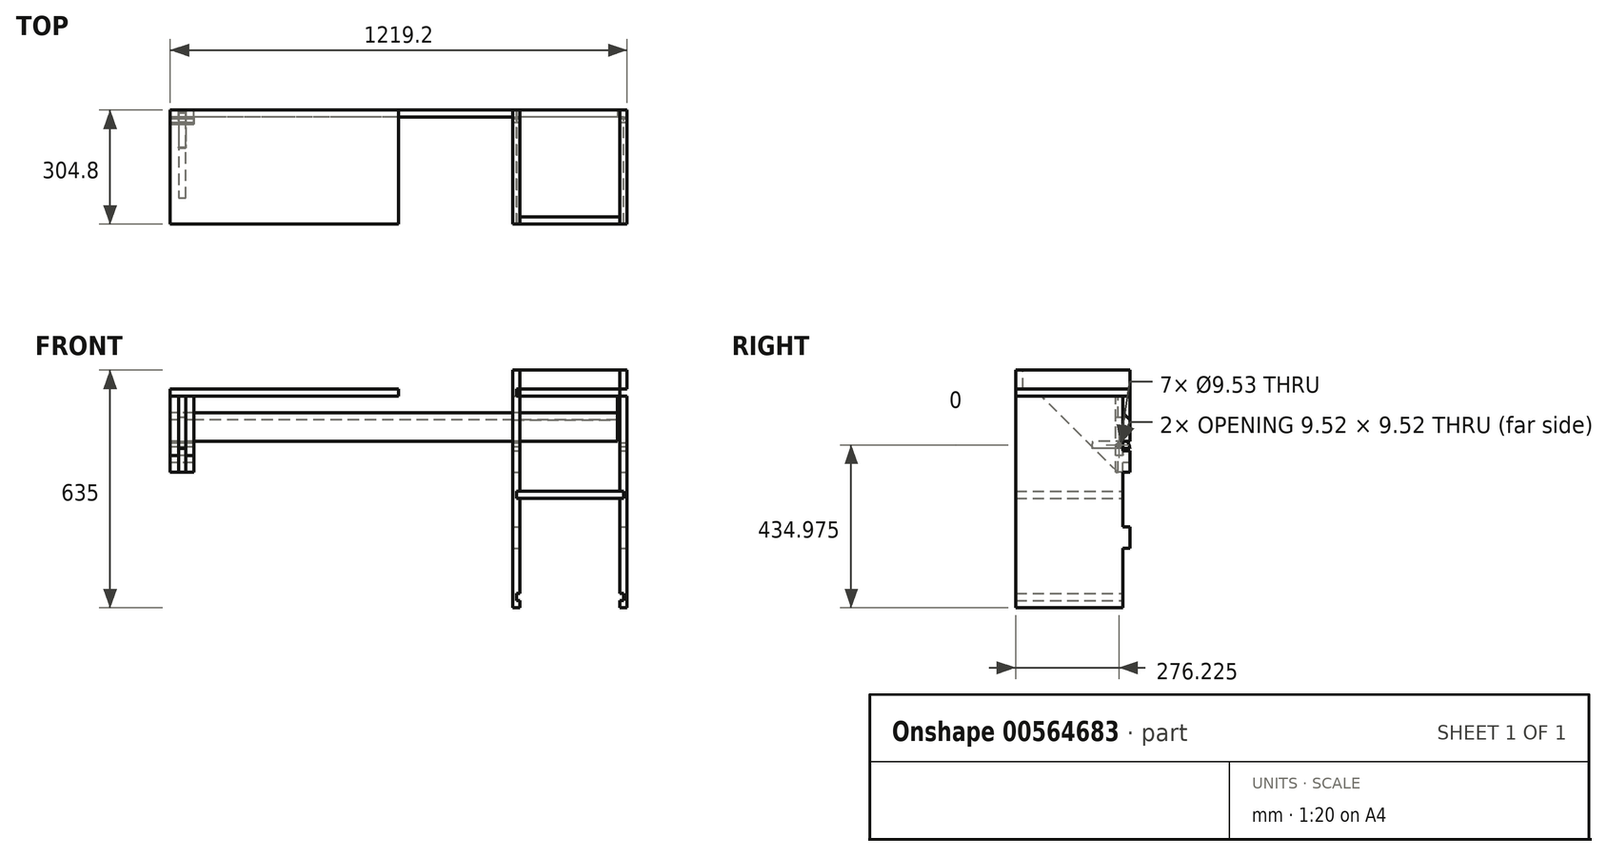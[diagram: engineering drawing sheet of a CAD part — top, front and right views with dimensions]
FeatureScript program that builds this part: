
annotation { "Feature Type Name" : "Feature", "Feature Type Description" : "" }
export const myFeature = defineFeature(function(context is Context, id is Id, definition is map)
    precondition{}
    {
        {
            var Q0;
            Q0=qCreatedBy(makeId("Right.planeOp"),FACE);
            var sketch = newSketch(context, id + "F0", { "sketchPlane" : qUnion([Q0])});
            skLineSegment(sketch, "E0", {"start": v(0, 0) * mm, "end": v(0, 57.15) * mm});
            skLineSegment(sketch, "E1", {"start": v(0, 57.15) * mm, "end": v(-19.05, 76.2) * mm});
            skLineSegment(sketch, "E2", {"start": v(-19.05, 76.2) * mm, "end": v(-19.05, 0) * mm});
            skLineSegment(sketch, "E3", {"start": v(-19.05, 0) * mm, "end": v(0, 0) * mm});
            skSolve(sketch);
        }
        {
            var Q0;
            Q0=makeQuery(id+"F0.imprint","IMPRINT",FACE,{"disambiguationData":[TD([[makeQuery(id+"F0.imprint","IMPRINT",EDGE,{"derivedFrom":sQuery(id+"F0.wireOp",EDGE,"E0")}),1.0]])]});
            extrude(context, id + "F1", {"entities" : qUnion([Q0]), "depth" : 1219.2 * mm, "offsetDistance" : 25.4 * mm});
        }
        {
            var Q0;
            Q0=qCreatedBy(makeId("Right.planeOp"),FACE);
            var sketch = newSketch(context, id + "F2", { "sketchPlane" : qUnion([Q0])});
            skLineSegment(sketch, "E4", {"start": v(0, 57.15) * mm, "end": v(0, 120.65) * mm});
            skLineSegment(sketch, "E5", {"start": v(0, 120.65) * mm, "end": v(-19.05, 120.65) * mm});
            skLineSegment(sketch, "E6", {"start": v(-19.05, 120.65) * mm, "end": v(-19.05, 76.2) * mm});
            skLineSegment(sketch, "E7", {"start": v(-19.05, 76.2) * mm, "end": v(0, 57.15) * mm});
            skSolve(sketch);
        }
        {
            var Q0;
            Q0=makeQuery(id+"F2.imprint","IMPRINT",FACE,{"disambiguationData":[TD([[makeQuery(id+"F2.imprint","IMPRINT",EDGE,{"derivedFrom":sQuery(id+"F2.wireOp",EDGE,"E4")}),1.0]])]});
            extrude(context, id + "F3", {"entities" : qUnion([Q0]), "depth" : 63.5 * mm, "offsetDistance" : 25.4 * mm});
        }
        {
            var Q0;
            Q0=makeQuery(id+"F3.opExtrude","SWEPT_FACE",FACE,{"disambiguationData":[OSD([sQuery(id+"F2.wireOp",EDGE,"E5")])]});
            var sketch = newSketch(context, id + "F4", { "sketchPlane" : qUnion([Q0])});
            skLineSegment(sketch, "E8.bottom", {"start": v(0, -19.05) * mm, "end": v(63.5, -19.05) * mm});
            skLineSegment(sketch, "E8.top", {"start": v(0, -38.1) * mm, "end": v(63.5, -38.1) * mm});
            skLineSegment(sketch, "E8.left", {"start": v(0, -19.05) * mm, "end": v(0, -38.1) * mm});
            skLineSegment(sketch, "E8.right", {"start": v(63.5, -19.05) * mm, "end": v(63.5, -38.1) * mm});
            skSolve(sketch);
        }
        {
            var Q0;
            Q0=makeQuery(id+"F4.imprint","IMPRINT",FACE,{"disambiguationData":[TD([[makeQuery(id+"F4.imprint","IMPRINT",EDGE,{"derivedFrom":sQuery(id+"F4.wireOp",EDGE,"E8.bottom")}),1.0]])]});
            extrude(context, id + "F5", {"entities" : qUnion([Q0]), "oppositeDirection" : true, "depth" : 203.2 * mm, "offsetDistance" : 25.4 * mm});
        }
        {
            var Q0;
            Q0=makeQuery(id+"F5.opExtrude","CAP_FACE",FACE,{"disambiguationData":[OSD([sQuery(id+"F4.wireOp",EDGE,"E8.bottom"),sQuery(id+"F4.wireOp",EDGE,"E8.top"),sQuery(id+"F4.wireOp",EDGE,"E8.left"),sQuery(id+"F4.wireOp",EDGE,"E8.right")])],"isStart":true});
            var sketch = newSketch(context, id + "F6", { "sketchPlane" : qUnion([Q0])});
            skLineSegment(sketch, "E9.bottom", {"start": v(22.23, -38.1) * mm, "end": v(41.28, -38.1) * mm});
            skLineSegment(sketch, "E9.top", {"start": v(22.23, -31.75) * mm, "end": v(41.28, -31.75) * mm});
            skLineSegment(sketch, "E9.left", {"start": v(22.23, -38.1) * mm, "end": v(22.23, -31.75) * mm});
            skLineSegment(sketch, "E9.right", {"start": v(41.28, -38.1) * mm, "end": v(41.28, -31.75) * mm});
            skSolve(sketch);
        }
        {
            var Q0;
            Q0=makeQuery(id+"F6.imprint","IMPRINT",FACE,{"disambiguationData":[TD([[makeQuery(id+"F6.imprint","IMPRINT",EDGE,{"derivedFrom":sQuery(id+"F6.wireOp",EDGE,"E9.bottom")}),1.0]])]});
            extrude(context, id + "F7", {"entities" : qUnion([Q0]), "operationType" : NewBodyOperationType.REMOVE, "endBound" : BoundingType.THROUGH_ALL, "oppositeDirection" : true, "depth" : 25.4 * mm, "offsetDistance" : 25.4 * mm});
        }
        {
            var Q0;
            Q0=makeQuery(id+"F7.boolean.opBoolean","COPY",FACE,{"derivedFrom":makeQuery(id+"F7.opExtrude","SWEPT_FACE",FACE,{"disambiguationData":[OSD([sQuery(id+"F6.wireOp",EDGE,"E9.right")])]})});
            var sketch = newSketch(context, id + "F8", { "sketchPlane" : qUnion([Q0])});
            skLineSegment(sketch, "E10", {"start": v(31.75, 120.65) * mm, "end": v(31.75, -82.55) * mm});
            skLineSegment(sketch, "E11", {"start": v(31.75, -82.55) * mm, "end": v(234.95, 120.65) * mm});
            skPoint(sketch, "E11.endSnap0", {"position": v(34.93, 120.65) * mm});
            skLineSegment(sketch, "E12", {"start": v(234.95, 120.65) * mm, "end": v(31.75, 120.65) * mm});
            skSolve(sketch);
        }
        {
            var Q0;
            Q0 = qSketchRegion(id + "F8", true);
            extrude(context, id + "F9", {"entities" : qUnion([Q0]), "depth" : 19.05 * mm, "offsetDistance" : 25.4 * mm});
        }
        {
            var Q0;
            Q0=qCreatedBy(makeId("Right.planeOp"),FACE);
            var sketch = newSketch(context, id + "F10", { "sketchPlane" : qUnion([Q0])});
            skLineSegment(sketch, "E13.bottom", {"start": v(0, 120.65) * mm, "end": v(-279.4, 120.65) * mm});
            skLineSegment(sketch, "E13.top", {"start": v(0, 139.7) * mm, "end": v(-279.4, 139.7) * mm});
            skLineSegment(sketch, "E13.left", {"start": v(0, 120.65) * mm, "end": v(0, 139.7) * mm});
            skLineSegment(sketch, "E13.right", {"start": v(-279.4, 120.65) * mm, "end": v(-279.4, 139.7) * mm});
            skSolve(sketch);
        }
        {
            var Q0;
            Q0=makeQuery(id+"F10.imprint","IMPRINT",FACE,{"disambiguationData":[TD([[makeQuery(id+"F10.imprint","IMPRINT",EDGE,{"derivedFrom":sQuery(id+"F10.wireOp",EDGE,"E13.bottom")}),-1.0]])]});
            extrude(context, id + "F11", {"entities" : qUnion([Q0]), "depth" : 609.6 * mm, "offsetDistance" : 25.4 * mm});
        }
        {
            var Q0;
            Q0=makeQuery(id+"F5.opExtrude","SWEPT_FACE",FACE,{"disambiguationData":[OSD([sQuery(id+"F4.wireOp",EDGE,"E8.bottom")])]});
            var sketch = newSketch(context, id + "F12", { "sketchPlane" : qUnion([Q0])});
            skLineSegment(sketch, "E14.bottom", {"start": v(-63.5, -82.55) * mm, "end": v(0, -82.55) * mm});
            skLineSegment(sketch, "E14.top", {"start": v(-63.5, -57.15) * mm, "end": v(0, -57.15) * mm});
            skLineSegment(sketch, "E14.left", {"start": v(-63.5, -82.55) * mm, "end": v(-63.5, -57.15) * mm});
            skLineSegment(sketch, "E14.right", {"start": v(0, -82.55) * mm, "end": v(0, -57.15) * mm});
            skSolve(sketch);
        }
        {
            var Q0;
            Q0=makeQuery(id+"F12.imprint","IMPRINT",FACE,{"disambiguationData":[TD([[makeQuery(id+"F12.imprint","IMPRINT",EDGE,{"derivedFrom":sQuery(id+"F12.wireOp",EDGE,"E14.bottom")}),1.0]])]});
            extrude(context, id + "F13", {"entities" : qUnion([Q0]), "depth" : 19.05 * mm, "offsetDistance" : 25.4 * mm});
        }
        {
            var Q0;
            Q0=makeQuery(id+"F11.opExtrude","SWEPT_FACE",FACE,{"disambiguationData":[OSD([sQuery(id+"F10.wireOp",EDGE,"E13.right")])]});
            extrude(context, id + "F14", {"entities" : qUnion([Q0]), "operationType" : NewBodyOperationType.ADD, "depth" : 25.4 * mm, "offsetDistance" : 25.4 * mm});
        }
        {
            var Q0;
            Q0=makeQuery(id+"F1.opExtrude","CAP_FACE",FACE,{"disambiguationData":[OSD([sQuery(id+"F0.wireOp",EDGE,"E0"),sQuery(id+"F0.wireOp",EDGE,"E1"),sQuery(id+"F0.wireOp",EDGE,"E2"),sQuery(id+"F0.wireOp",EDGE,"E3")])],"isStart":false});
            var sketch = newSketch(context, id + "F15", { "sketchPlane" : qUnion([Q0])});
            skLineSegment(sketch, "E15", {"start": v(0, 57.15) * mm, "end": v(-19.05, 76.2) * mm});
            skLineSegment(sketch, "E16", {"start": v(-19.05, 76.2) * mm, "end": v(-19.05, 120.65) * mm});
            skLineSegment(sketch, "E17", {"start": v(-19.05, 120.65) * mm, "end": v(0, 120.65) * mm});
            skLineSegment(sketch, "E18", {"start": v(0, 120.65) * mm, "end": v(0, 57.15) * mm});
            skSolve(sketch);
        }
        {
            var Q0;
            Q0=makeQuery(id+"F15.imprint","IMPRINT",FACE,{"disambiguationData":[TD([[makeQuery(id+"F15.imprint","IMPRINT",EDGE,{"derivedFrom":sQuery(id+"F15.wireOp",EDGE,"E15")}),-1.0]])]});
            extrude(context, id + "F16", {"entities" : qUnion([Q0]), "oppositeDirection" : true, "depth" : 304.8 * mm, "offsetDistance" : 25.4 * mm});
        }
        {
            var Q0;
            Q0=makeQuery(id+"F16.opExtrude","CAP_FACE",FACE,{"disambiguationData":[OSD([sQuery(id+"F15.wireOp",EDGE,"E15"),sQuery(id+"F15.wireOp",EDGE,"E16"),sQuery(id+"F15.wireOp",EDGE,"E17"),sQuery(id+"F15.wireOp",EDGE,"E18")])],"isStart":true});
            var sketch = newSketch(context, id + "F17", { "sketchPlane" : qUnion([Q0])});
            skLineSegment(sketch, "E19.bottom", {"start": v(0, 120.65) * mm, "end": v(-304.8, 120.65) * mm});
            skLineSegment(sketch, "E19.top", {"start": v(0, 139.7) * mm, "end": v(-304.8, 139.7) * mm});
            skLineSegment(sketch, "E19.left", {"start": v(0, 120.65) * mm, "end": v(0, 139.7) * mm});
            skLineSegment(sketch, "E19.right", {"start": v(-304.8, 120.65) * mm, "end": v(-304.8, 139.7) * mm});
            skSolve(sketch);
        }
        {
            var Q0;
            Q0=makeQuery(id+"F17.imprint","IMPRINT",FACE,{"disambiguationData":[TD([[makeQuery(id+"F17.imprint","IMPRINT",EDGE,{"derivedFrom":sQuery(id+"F17.wireOp",EDGE,"E19.top")}),1.0]])]});
            extrude(context, id + "F18", {"entities" : qUnion([Q0]), "oppositeDirection" : true, "depth" : 304.8 * mm, "offsetDistance" : 25.4 * mm});
        }
        {
            var Q0;
            Q0=makeQuery(id+"F16.opExtrude","CAP_FACE",FACE,{"disambiguationData":[OSD([sQuery(id+"F15.wireOp",EDGE,"E15"),sQuery(id+"F15.wireOp",EDGE,"E16"),sQuery(id+"F15.wireOp",EDGE,"E17"),sQuery(id+"F15.wireOp",EDGE,"E18")])],"isStart":true});
            var sketch = newSketch(context, id + "F19", { "sketchPlane" : qUnion([Q0])});
            skLineSegment(sketch, "E20.bottom", {"start": v(-304.8, 165.1) * mm, "end": v(0, 165.1) * mm});
            skLineSegment(sketch, "E20.top", {"start": v(-304.8, -444.5) * mm, "end": v(0, -444.5) * mm});
            skLineSegment(sketch, "E20.left", {"start": v(-304.8, 165.1) * mm, "end": v(-304.8, -444.5) * mm});
            skLineSegment(sketch, "E20.right", {"start": v(0, 165.1) * mm, "end": v(0, -444.5) * mm});
            skSolve(sketch);
        }
        {
            var Q0;
            {var subQ1=makeQuery(id+"F16.opExtrude","CAP_EDGE",EDGE,{"disambiguationData":[OSD([sQuery(id+"F15.wireOp",EDGE,"E15")])],"isStart":true});Q0=makeQuery(id+"F19.imprint","IMPRINT",FACE,{"disambiguationData":[TD([[makeQuery(id+"F19.imprint","IMPRINT",EDGE,{"derivedFrom":subQ1}),-1.0]])]});}
            var Q1;
            {var subQ2=sQuery(id+"F19.wireOp",EDGE,"E20.bottom");Q1=makeQuery(id+"F19.imprint","IMPRINT",FACE,{"disambiguationData":[TD([[makeQuery(id+"F19.imprint","IMPRINT",EDGE,{"derivedFrom":subQ2}),-1.0]])]});}
            extrude(context, id + "F20", {"entities" : qUnion([Q0, Q1]), "oppositeDirection" : true, "depth" : 19.05 * mm, "offsetDistance" : 25.4 * mm});
        }
        {
            var Q0;
            Q0=makeQuery(id+"F20.opExtrude","SWEPT_FACE",FACE,{"disambiguationData":[OSD([sQuery(id+"F19.wireOp",EDGE,"E20.bottom")])]});
            extrude(context, id + "F21", {"entities" : qUnion([Q0]), "operationType" : NewBodyOperationType.ADD, "depth" : 25.4 * mm, "offsetDistance" : 25.4 * mm});
        }
        {
            var Q0;
            {var subQ0=sQuery(id+"F19.wireOp",EDGE,"E20.bottom");Q0=makeQuery(id+"F21.boolean.opBoolean","MERGE",FACE,{"derivedFrom":[makeQuery(id+"F20.opExtrude","CAP_FACE",FACE,{"disambiguationData":[OSD([subQ0,sQuery(id+"F19.wireOp",EDGE,"E20.top"),sQuery(id+"F19.wireOp",EDGE,"E20.left"),sQuery(id+"F19.wireOp",EDGE,"E20.right")])],"isStart":true}),makeQuery(id+"F21.opExtrude","SWEPT_FACE",FACE,{"disambiguationData":[OSD([subQ0]),TDD([makeQuery(id+"F20.opExtrude","CAP_EDGE",EDGE,{"disambiguationData":[OSD([subQ0])],"isStart":true})])]})]});}
            var sketch = newSketch(context, id + "F22", { "sketchPlane" : qUnion([Q0])});
            skLineSegment(sketch, "E21.bottom", {"start": v(0, 120.65) * mm, "end": v(-19.05, 120.65) * mm});
            skLineSegment(sketch, "E21.top", {"start": v(0, -25.4) * mm, "end": v(-19.05, -25.4) * mm});
            skLineSegment(sketch, "E21.left", {"start": v(0, 120.65) * mm, "end": v(0, -25.4) * mm});
            skLineSegment(sketch, "E21.right", {"start": v(-19.05, 120.65) * mm, "end": v(-19.05, -25.4) * mm});
            skLineSegment(sketch, "E22.bottom", {"start": v(0, -82.55) * mm, "end": v(-19.05, -82.55) * mm});
            skLineSegment(sketch, "E22.top", {"start": v(0, -228.6) * mm, "end": v(-19.05, -228.6) * mm});
            skLineSegment(sketch, "E22.left", {"start": v(0, -82.55) * mm, "end": v(0, -228.6) * mm});
            skLineSegment(sketch, "E22.right", {"start": v(-19.05, -82.55) * mm, "end": v(-19.05, -228.6) * mm});
            skLineSegment(sketch, "E23.bottom", {"start": v(0, -285.75) * mm, "end": v(-19.05, -285.75) * mm});
            skLineSegment(sketch, "E23.top", {"start": v(0, -444.5) * mm, "end": v(-19.05, -444.5) * mm});
            skLineSegment(sketch, "E23.left", {"start": v(0, -285.75) * mm, "end": v(0, -444.5) * mm});
            skLineSegment(sketch, "E23.right", {"start": v(-19.05, -285.75) * mm, "end": v(-19.05, -444.5) * mm});
            skSolve(sketch);
        }
        {
            var Q0;
            Q0 = qSketchRegion(id + "F22", true);
            extrude(context, id + "F23", {"entities" : qUnion([Q0]), "operationType" : NewBodyOperationType.REMOVE, "oppositeDirection" : true, "depth" : 25.4 * mm, "offsetDistance" : 25.4 * mm});
        }
        {
            var Q0;
            Q0=makeQuery(id+"F18.opExtrude","CAP_FACE",FACE,{"disambiguationData":[OSD([sQuery(id+"F17.wireOp",EDGE,"E19.bottom"),sQuery(id+"F17.wireOp",EDGE,"E19.top"),sQuery(id+"F17.wireOp",EDGE,"E19.left"),sQuery(id+"F17.wireOp",EDGE,"E19.right")])],"isStart":true});
            extrude(context, id + "F24", {"entities" : qUnion([Q0]), "operationType" : NewBodyOperationType.REMOVE, "oppositeDirection" : true, "depth" : 9.52 * mm, "offsetDistance" : 25.4 * mm});
        }
        {
            var Q0;
            Q0=makeQuery(id+"F18.opExtrude","CAP_FACE",FACE,{"disambiguationData":[OSD([sQuery(id+"F17.wireOp",EDGE,"E19.bottom"),sQuery(id+"F17.wireOp",EDGE,"E19.top"),sQuery(id+"F17.wireOp",EDGE,"E19.left"),sQuery(id+"F17.wireOp",EDGE,"E19.right")])],"isStart":false});
            extrude(context, id + "F25", {"entities" : qUnion([Q0]), "operationType" : NewBodyOperationType.REMOVE, "oppositeDirection" : true, "depth" : 9.52 * mm, "offsetDistance" : 25.4 * mm});
        }
        {
            var Q0;
            Q0=makeQuery(id+"F20.opExtrude","SWEPT_BODY",BODY,{"disambiguationData":[OSD([sQuery(id+"F19.wireOp",EDGE,"E20.bottom"),sQuery(id+"F19.wireOp",EDGE,"E20.top"),sQuery(id+"F19.wireOp",EDGE,"E20.left"),sQuery(id+"F19.wireOp",EDGE,"E20.right")])]});
            transform(context, id + "F26", {"entities" : qUnion([Q0]), "transformType" : TransformType.TRANSLATION_3D, "dx" : -285.75 * mm, "dy" : 0 * mm, "dz" : 0 * mm, "makeCopy" : true});
        }
        {
            var Q0;
            {var subQ0=sQuery(id+"F19.wireOp",EDGE,"E20.bottom");var subQ1=sQuery(id+"F19.wireOp",EDGE,"E20.right");Q0=makeQuery(id+"F23.boolean.opBoolean","SPLIT",FACE,{"disambiguationData":[TD([makeQuery(id+"F21.opExtrude","CAP_FACE",FACE,{"disambiguationData":[OSD([subQ0])],"isStart":false})])],"derivedFrom":makeQuery(id+"F21.boolean.opBoolean","MERGE",FACE,{"derivedFrom":[makeQuery(id+"F20.opExtrude","SWEPT_FACE",FACE,{"disambiguationData":[OSD([subQ1])]}),makeQuery(id+"F21.opExtrude","SWEPT_FACE",FACE,{"disambiguationData":[OSD([subQ0,subQ1])]})]})});}
            var sketch = newSketch(context, id + "F27", { "sketchPlane" : qUnion([Q0])});
            skLineSegment(sketch, "E24.bottom", {"start": v(-1200.15, 120.65) * mm, "end": v(-1209.67, 120.65) * mm});
            skLineSegment(sketch, "E24.top", {"start": v(-1200.15, 139.7) * mm, "end": v(-1209.67, 139.7) * mm});
            skLineSegment(sketch, "E24.left", {"start": v(-1200.15, 120.65) * mm, "end": v(-1200.15, 139.7) * mm});
            skLineSegment(sketch, "E24.right", {"start": v(-1209.67, 120.65) * mm, "end": v(-1209.67, 139.7) * mm});
            skLineSegment(sketch, "E25.0.1.0", {"start": v(-1209.67, -152.4) * mm, "end": v(-1209.67, -133.35) * mm});
            skLineSegment(sketch, "E25.0.1.1", {"start": v(-1200.15, -133.35) * mm, "end": v(-1209.67, -133.35) * mm});
            skLineSegment(sketch, "E25.0.1.2", {"start": v(-1200.15, -152.4) * mm, "end": v(-1200.15, -133.35) * mm});
            skLineSegment(sketch, "E25.0.1.3", {"start": v(-1200.15, -152.4) * mm, "end": v(-1209.67, -152.4) * mm});
            skLineSegment(sketch, "E25.0.2.0", {"start": v(-1209.67, -425.45) * mm, "end": v(-1209.67, -406.4) * mm});
            skLineSegment(sketch, "E25.0.2.1", {"start": v(-1200.15, -406.4) * mm, "end": v(-1209.67, -406.4) * mm});
            skLineSegment(sketch, "E25.0.2.2", {"start": v(-1200.15, -425.45) * mm, "end": v(-1200.15, -406.4) * mm});
            skLineSegment(sketch, "E25.0.2.3", {"start": v(-1200.15, -425.45) * mm, "end": v(-1209.67, -425.45) * mm});
            skLineSegment(sketch, "E25.direction1", {"start": v(-1209.67, 120.65) * mm, "end": v(-1184.27, 120.65) * mm, "construction": true});
            skLineSegment(sketch, "E25.direction2", {"start": v(-1209.67, 120.65) * mm, "end": v(-1209.67, -152.4) * mm, "construction": true});
            skSolve(sketch);
        }
        {
            var Q0;
            Q0 = qSketchRegion(id + "F27", true);
            extrude(context, id + "F28", {"entities" : qUnion([Q0]), "operationType" : NewBodyOperationType.REMOVE, "endBound" : BoundingType.THROUGH_ALL, "oppositeDirection" : true, "depth" : 25.4 * mm, "offsetDistance" : 25.4 * mm});
        }
        {
            var Q0;
            {var subQ0=sQuery(id+"F19.wireOp",EDGE,"E20.bottom");var subQ1=sQuery(id+"F19.wireOp",EDGE,"E20.right");Q0=makeQuery(id+"F26.opPattern","COPY",FACE,{"derivedFrom":makeQuery(id+"F23.boolean.opBoolean","SPLIT",FACE,{"disambiguationData":[TD([makeQuery(id+"F21.opExtrude","CAP_FACE",FACE,{"disambiguationData":[OSD([subQ0])],"isStart":false})])],"derivedFrom":makeQuery(id+"F21.boolean.opBoolean","MERGE",FACE,{"derivedFrom":[makeQuery(id+"F20.opExtrude","SWEPT_FACE",FACE,{"disambiguationData":[OSD([subQ1])]}),makeQuery(id+"F21.opExtrude","SWEPT_FACE",FACE,{"disambiguationData":[OSD([subQ0,subQ1])]})]})}),"instanceName":"1"});}
            var sketch = newSketch(context, id + "F29", { "sketchPlane" : qUnion([Q0])});
            skLineSegment(sketch, "E26.bottom", {"start": v(-933.45, 120.65) * mm, "end": v(-923.93, 120.65) * mm});
            skLineSegment(sketch, "E26.top", {"start": v(-933.45, 139.7) * mm, "end": v(-923.93, 139.7) * mm});
            skLineSegment(sketch, "E26.left", {"start": v(-933.45, 120.65) * mm, "end": v(-933.45, 139.7) * mm});
            skLineSegment(sketch, "E26.right", {"start": v(-923.93, 120.65) * mm, "end": v(-923.93, 139.7) * mm});
            skLineSegment(sketch, "E27.0.1.0", {"start": v(-933.45, -152.4) * mm, "end": v(-933.45, -133.35) * mm});
            skLineSegment(sketch, "E27.0.1.1", {"start": v(-923.93, -152.4) * mm, "end": v(-923.93, -133.35) * mm});
            skLineSegment(sketch, "E27.0.1.2", {"start": v(-933.45, -133.35) * mm, "end": v(-923.93, -133.35) * mm});
            skLineSegment(sketch, "E27.0.1.3", {"start": v(-933.45, -152.4) * mm, "end": v(-923.93, -152.4) * mm});
            skLineSegment(sketch, "E27.0.2.0", {"start": v(-933.45, -425.45) * mm, "end": v(-933.45, -406.4) * mm});
            skLineSegment(sketch, "E27.0.2.1", {"start": v(-923.93, -425.45) * mm, "end": v(-923.93, -406.4) * mm});
            skLineSegment(sketch, "E27.0.2.2", {"start": v(-933.45, -406.4) * mm, "end": v(-923.93, -406.4) * mm});
            skLineSegment(sketch, "E27.0.2.3", {"start": v(-933.45, -425.45) * mm, "end": v(-923.93, -425.45) * mm});
            skLineSegment(sketch, "E27.direction1", {"start": v(-933.45, 120.65) * mm, "end": v(-908.05, 120.65) * mm, "construction": true});
            skLineSegment(sketch, "E27.direction2", {"start": v(-933.45, 120.65) * mm, "end": v(-933.45, -152.4) * mm, "construction": true});
            skSolve(sketch);
        }
        {
            var Q0;
            Q0 = qSketchRegion(id + "F29", true);
            extrude(context, id + "F30", {"entities" : qUnion([Q0]), "operationType" : NewBodyOperationType.REMOVE, "endBound" : BoundingType.THROUGH_ALL, "oppositeDirection" : true, "depth" : 25.4 * mm, "offsetDistance" : 25.4 * mm});
        }
        {
            var Q0;
            Q0=makeQuery(id+"F23.boolean.opBoolean","COPY",FACE,{"derivedFrom":makeQuery(id+"F23.opExtrude","SWEPT_FACE",FACE,{"disambiguationData":[OSD([sQuery(id+"F22.wireOp",EDGE,"E22.right")])]})});
            var sketch = newSketch(context, id + "F31", { "sketchPlane" : qUnion([Q0])});
            skLineSegment(sketch, "E28.bottom", {"start": v(-1209.67, -133.35) * mm, "end": v(-923.93, -133.35) * mm});
            skLineSegment(sketch, "E28.top", {"start": v(-1209.67, -152.4) * mm, "end": v(-923.93, -152.4) * mm});
            skLineSegment(sketch, "E28.left", {"start": v(-1209.67, -133.35) * mm, "end": v(-1209.67, -152.4) * mm});
            skLineSegment(sketch, "E28.right", {"start": v(-923.93, -133.35) * mm, "end": v(-923.93, -152.4) * mm});
            skSolve(sketch);
        }
        {
            var Q0;
            {var subQ0=sQuery(id+"F31.wireOp",EDGE,"E28.left");Q0=makeQuery(id+"F31.imprint","IMPRINT",FACE,{"disambiguationData":[TD([[makeQuery(id+"F31.imprint","IMPRINT",EDGE,{"derivedFrom":subQ0}),1.0]])]});}
            var Q1;
            {var subQ0=sQuery(id+"F19.wireOp",EDGE,"E20.left");Q1=makeQuery(id+"F26.opPattern","COPY",FACE,{"derivedFrom":makeQuery(id+"F21.boolean.opBoolean","MERGE",FACE,{"derivedFrom":[makeQuery(id+"F20.opExtrude","SWEPT_FACE",FACE,{"disambiguationData":[OSD([subQ0])]}),makeQuery(id+"F21.opExtrude","SWEPT_FACE",FACE,{"disambiguationData":[OSD([sQuery(id+"F19.wireOp",EDGE,"E20.bottom"),subQ0])]})]}),"instanceName":"1"});}
            extrude(context, id + "F32", {"entities" : qUnion([Q0]), "endBound" : BoundingType.UP_TO_SURFACE, "oppositeDirection" : true, "depth" : 25.4 * mm, "endBoundEntityFace" : qUnion([Q1]), "offsetDistance" : 25.4 * mm});
        }
        {
            var Q0;
            {var subQ0=sQuery(id+"F19.wireOp",EDGE,"E20.right");var subQ1=sQuery(id+"F19.wireOp",EDGE,"E20.bottom");var subQ2=sQuery(id+"F19.wireOp",EDGE,"E20.left");Q0=makeQuery(id+"F28.boolean.opBoolean","SPLIT",FACE,{"disambiguationData":[TD([makeQuery(id+"F21.opExtrude","CAP_FACE",FACE,{"disambiguationData":[OSD([subQ1])],"isStart":false})])],"derivedFrom":makeQuery(id+"F21.boolean.opBoolean","MERGE",FACE,{"derivedFrom":[makeQuery(id+"F20.opExtrude","CAP_FACE",FACE,{"disambiguationData":[OSD([subQ1,sQuery(id+"F19.wireOp",EDGE,"E20.top"),subQ2,subQ0])],"isStart":false}),makeQuery(id+"F21.opExtrude","SWEPT_FACE",FACE,{"disambiguationData":[OSD([subQ1]),TDD([makeQuery(id+"F20.opExtrude","CAP_EDGE",EDGE,{"disambiguationData":[OSD([subQ1])],"isStart":false})])]})]})});}
            var sketch = newSketch(context, id + "F33", { "sketchPlane" : qUnion([Q0])});
            skLineSegment(sketch, "E29.bottom", {"start": v(304.8, 190.5) * mm, "end": v(285.75, 190.5) * mm});
            skLineSegment(sketch, "E29.top", {"start": v(304.8, 139.7) * mm, "end": v(285.75, 139.7) * mm});
            skLineSegment(sketch, "E29.left", {"start": v(304.8, 190.5) * mm, "end": v(304.8, 139.7) * mm});
            skLineSegment(sketch, "E29.right", {"start": v(285.75, 190.5) * mm, "end": v(285.75, 139.7) * mm});
            skSolve(sketch);
        }
        {
            var Q0;
            Q0 = qSketchRegion(id + "F33", true);
            extrude(context, id + "F34", {"entities" : qUnion([Q0]), "endBound" : BoundingType.UP_TO_NEXT, "depth" : 25.4 * mm, "offsetDistance" : 25.4 * mm});
        }
        {
            var Q0;
            Q0=makeQuery(id+"F3.opExtrude","SWEPT_FACE",FACE,{"disambiguationData":[OSD([sQuery(id+"F2.wireOp",EDGE,"E5")])]});
            var sketch = newSketch(context, id + "F35", { "sketchPlane" : qUnion([Q0])});
            skLineSegment(sketch, "E30.bottom", {"start": v(0, -19.05) * mm, "end": v(63.5, -19.05) * mm});
            skLineSegment(sketch, "E30.top", {"start": v(0, -38.1) * mm, "end": v(63.5, -38.1) * mm});
            skLineSegment(sketch, "E30.left", {"start": v(0, -19.05) * mm, "end": v(0, -38.1) * mm});
            skLineSegment(sketch, "E30.right", {"start": v(63.5, -19.05) * mm, "end": v(63.5, -38.1) * mm});
            skSolve(sketch);
        }
        {
            var Q0;
            Q0 = qSketchRegion(id + "F35", true);
            extrude(context, id + "F36", {"entities" : qUnion([Q0]), "oppositeDirection" : true, "depth" : 158.75 * mm, "offsetDistance" : 25.4 * mm});
        }
        {
            var Q0;
            Q0=makeQuery(id+"F36.opExtrude","SWEPT_FACE",FACE,{"disambiguationData":[OSD([sQuery(id+"F35.wireOp",EDGE,"E30.top")])]});
            var sketch = newSketch(context, id + "F37", { "sketchPlane" : qUnion([Q0])});
            skLineSegment(sketch, "E31.bottom", {"start": v(22.23, -38.1) * mm, "end": v(41.28, -38.1) * mm});
            skLineSegment(sketch, "E31.top", {"start": v(22.23, 63.5) * mm, "end": v(41.28, 63.5) * mm});
            skLineSegment(sketch, "E31.left", {"start": v(22.23, -38.1) * mm, "end": v(22.23, 63.5) * mm});
            skLineSegment(sketch, "E31.right", {"start": v(41.28, -38.1) * mm, "end": v(41.28, 63.5) * mm});
            skSolve(sketch);
        }
        {
            var Q0;
            Q0=makeQuery(id+"F37.imprint","IMPRINT",FACE,{"disambiguationData":[TD([[makeQuery(id+"F37.imprint","IMPRINT",EDGE,{"derivedFrom":sQuery(id+"F37.wireOp",EDGE,"E31.bottom")}),1.0]])]});
            extrude(context, id + "F38", {"entities" : qUnion([Q0]), "operationType" : NewBodyOperationType.REMOVE, "endBound" : BoundingType.THROUGH_ALL, "oppositeDirection" : true, "depth" : 25.4 * mm, "offsetDistance" : 25.4 * mm});
        }
        {
            var Q0;
            Q0=makeQuery(id+"F38.boolean.opBoolean","COPY",FACE,{"derivedFrom":makeQuery(id+"F38.opExtrude","SWEPT_FACE",FACE,{"disambiguationData":[OSD([sQuery(id+"F37.wireOp",EDGE,"E31.right")])]})});
            var sketch = newSketch(context, id + "F39", { "sketchPlane" : qUnion([Q0])});
            skLineSegment(sketch, "E32.bottom", {"start": v(7.28, 0) * mm, "end": v(99.07, 0) * mm});
            skLineSegment(sketch, "E32.top", {"start": v(0, -19.05) * mm, "end": v(101.6, -19.05) * mm});
            skArc(sketch, "E33", {"start": v(7.28, 0) * mm, "mid": v(1.88, -8.85) * mm, "end": v(0, -19.05) * mm});
            skPoint(sketch, "E33.centerSnap0", {"position": v(28.57, -38.1) * mm});
            skArc(sketch, "E34", {"start": v(101.6, -19.05) * mm, "mid": v(100.97, -9.44) * mm, "end": v(99.07, 0) * mm});
            skSolve(sketch);
        }
        {
            var Q0;
            {var subQ0=sQuery(id+"F39.wireOp",EDGE,"E34");Q0=makeQuery(id+"F39.imprint","IMPRINT",FACE,{"disambiguationData":[TD([[makeQuery(id+"F39.imprint","IMPRINT",EDGE,{"derivedFrom":subQ0}),1.0]])]});}
            var Q1;
            {var subQ0=sQuery(id+"F39.wireOp",EDGE,"E32.bottom");var subQ1=sQuery(id+"F37.wireOp",EDGE,"E31.right");var subQ4=makeQuery(id+"F38.boolean.opBoolean","COPY",EDGE,{"derivedFrom":makeQuery(id+"F38.opExtrude","CAP_EDGE",EDGE,{"disambiguationData":[OSD([subQ1])],"isStart":true})});var subQ5=makeQuery(id+"F39.imprint","INTERSECT",VERTEX,{"derivedFrom":[subQ4,subQ0]});Q1=makeQuery(id+"F39.imprint","IMPRINT",FACE,{"disambiguationData":[TD([[makeQuery(id+"F39.imprint","IMPRINT",EDGE,{"disambiguationData":[TD([[subQ5,1.0]])],"derivedFrom":subQ4}),1.0]])]});}
            var Q2;
            {var subQ0=sQuery(id+"F39.wireOp",EDGE,"E33");Q2=makeQuery(id+"F39.imprint","IMPRINT",FACE,{"disambiguationData":[TD([[makeQuery(id+"F39.imprint","IMPRINT",EDGE,{"derivedFrom":subQ0}),1.0]])]});}
            extrude(context, id + "F40", {"entities" : qUnion([Q0, Q1, Q2]), "depth" : 19.05 * mm, "offsetDistance" : 25.4 * mm});
        }
        {
            var Q0;
            Q0=makeQuery(id+"F36.opExtrude","SWEPT_FACE",FACE,{"disambiguationData":[OSD([sQuery(id+"F35.wireOp",EDGE,"E30.left")])]});
            var sketch = newSketch(context, id + "F41", { "sketchPlane" : qUnion([Q0])});
            skCircle(sketch, "E35", {"center": v(28.57, -9.52) * mm, "radius": 4.76 * mm});
            skPoint(sketch, "E35.centerSnap0", {"position": v(28.57, -38.1) * mm});
            skSolve(sketch);
        }
        {
            var Q0;
            Q0=makeQuery(id+"F41.imprint","IMPRINT",FACE,{"disambiguationData":[TD([[makeQuery(id+"F41.imprint","IMPRINT",EDGE,{"derivedFrom":sQuery(id+"F41.wireOp",EDGE,"E35")}),1.0]])]});
            extrude(context, id + "F42", {"entities" : qUnion([Q0]), "operationType" : NewBodyOperationType.REMOVE, "endBound" : BoundingType.THROUGH_ALL, "oppositeDirection" : true, "depth" : 25.4 * mm, "offsetDistance" : 25.4 * mm});
        }
        {
            var Q0;
            Q0=makeQuery(id+"F36.opExtrude","SWEPT_FACE",FACE,{"disambiguationData":[OSD([sQuery(id+"F35.wireOp",EDGE,"E30.left")])]});
            var sketch = newSketch(context, id + "F43", { "sketchPlane" : qUnion([Q0])});
            skCircle(sketch, "E36", {"center": v(28.57, -9.52) * mm, "radius": 4.76 * mm});
            skSolve(sketch);
        }
        {
            var Q0;
            Q0 = qSketchRegion(id + "F43", true);
            var Q1;
            Q1=makeQuery(id+"F36.opExtrude","SWEPT_FACE",FACE,{"disambiguationData":[OSD([sQuery(id+"F35.wireOp",EDGE,"E30.right")])]});
            extrude(context, id + "F44", {"entities" : qUnion([Q0]), "endBound" : BoundingType.UP_TO_SURFACE, "oppositeDirection" : true, "depth" : 25.4 * mm, "endBoundEntityFace" : qUnion([Q1]), "offsetDistance" : 25.4 * mm});
        }
    });
